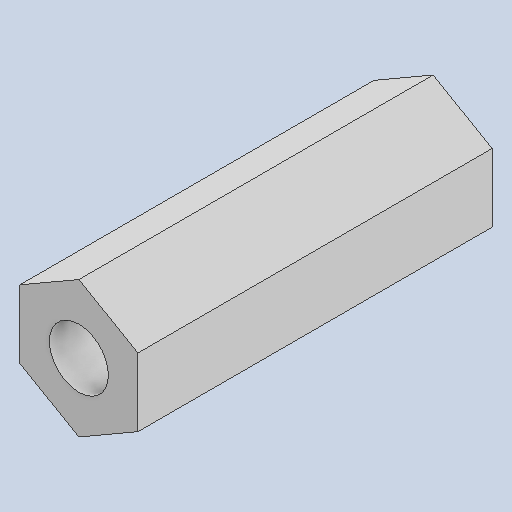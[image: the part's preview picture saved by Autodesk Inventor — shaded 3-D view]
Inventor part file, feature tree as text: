
AUTODESK INVENTOR PART (.ipt)
format: ipt  version: 2024.2 (Build 282272000, 272)  size: 82,432 bytes
history: native  units: in
note: dims shown in document units (in); Inventor stores cm internally (conversion verified against a paired STEP export)
features: extrude x1
ambient origin geometry x8: Origin, YZ Plane, XZ Plane, XY Plane, X Axis, Y Axis, Z Axis, Center Point
bodies: Solid1 (feature_tree)
feature tree (1):
  extrude  "Extrude1"  [1 undecoded]
note: 1 required parameter value undecoded (feature->parameter linkage not recoverable at this tier; creation-order binding heuristic only, values carry confidence <= 0.55)
